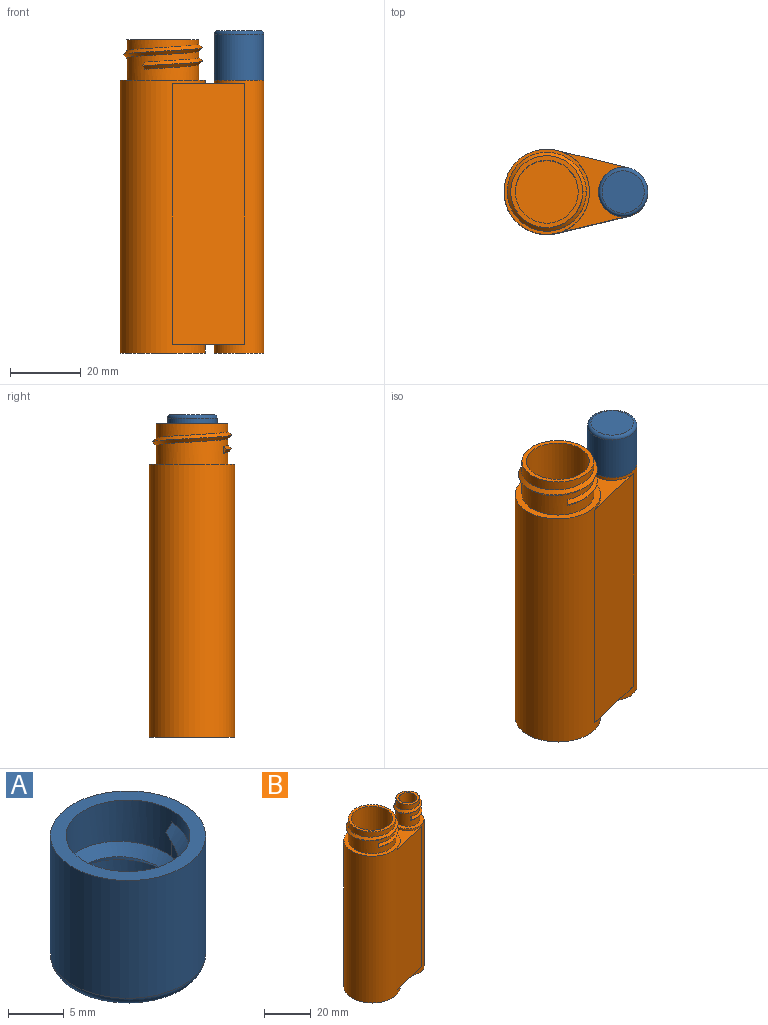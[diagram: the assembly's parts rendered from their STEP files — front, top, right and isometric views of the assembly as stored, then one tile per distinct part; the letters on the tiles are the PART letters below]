
ASSEMBLY  parts=2 mates=1
PART A: 12 faces, bbox 15.2x15.2x14 mm
  f0: cylinder r=6.99mm len=13.97mm, axis (0,0,-1), area 569.2mm2, adj f2,f3
  f1: plane 11.97x11.97mm, normal (0,0,-1), area 112.5mm2, adj f2
  f2: torus R=5.98mm, axis (0,0,1), area 65.4mm2, adj f0,f1
  f3: plane 13.97x13.97mm, normal (0,0,1), area 55.5mm2, adj f0,f11
  f4: plane 1.39x0.81mm, normal (0,1,0), area 0.5mm2, adj f5,f8,f11
  f5: bspline ~3.23x2.71mm, area 4.3mm2, adj f4,f6,f8,f10,f11
  f6: bspline ~12.89x11.16mm, area 55.6mm2, adj f5,f7,f8,f10
  f7: plane 2x0.87mm, normal (-0.87,0.5,0), area 1mm2, adj f6,f8,f10
  f8: bspline ~12.89x11.16mm, area 59.9mm2, adj f4,f5,f6,f7,f10,f11
  f9: plane 11.16x11.16mm, normal (0,0,1), area 97.8mm2, adj f10
  f10: cylinder r=5.58mm len=11.16mm, axis (0,0,-1), area 197mm2, adj f5,f6,f7,f8,f9,f11
  f11: cylinder r=5.58mm len=11.16mm, axis (0,0,-1), area 148.6mm2, adj f3,f4,f5,f8,f10
PART B: 28 faces, bbox 40.6x25.8x88.6 mm
  f0: cylinder r=6.99mm len=77.2mm, axis (0,0,-1), area 1527.3mm2, adj f2,f4,f5,f6,f7,f11
  f1: cylinder r=12.06mm len=77.2mm, axis (0,0,-1), area 3482.5mm2, adj f2,f3,f5,f6,f7,f8
  f2: plane 23.45x20.47mm, normal (0,0,1), area 117.4mm2, adj f0,f1,f6,f7
  f3: plane 24.13x24.13mm, normal (0,0,-1), area 457.3mm2, adj f1
  f4: plane 13.97x13.97mm, normal (0,0,-1), area 153.3mm2, adj f0
  f5: plane 23.45x20.47mm, normal (0,0,-1), area 117.4mm2, adj f0,f1,f6,f7
  f6: plane 73.66x20.37mm, normal (0.24,0.97,0), area 1545.7mm2, adj f0,f1,f2,f5
  f7: plane 73.66x20.42mm, normal (0.23,-0.97,0), area 1545.7mm2, adj f0,f1,f2,f5
  f8: plane 24.13x24.13mm, normal (0,0,1), area 133mm2, adj f1,f9
  f9: cylinder r=10.16mm len=20.32mm, axis (0,0,1), area 356.7mm2, adj f8,f10,f15,f16,f17
  f10: cylinder r=10.16mm len=20.32mm, axis (0,0,1), area 202.7mm2, adj f9,f14,f16,f22
  f11: plane 13.97x13.97mm, normal (0,0,1), area 72.2mm2, adj f0,f12
  f12: cylinder r=5.08mm len=10.16mm, axis (0,0,1), area 178.4mm2, adj f11,f13,f19,f20,f21
  f13: cylinder r=5.08mm len=10.16mm, axis (0,0,1), area 101.3mm2, adj f12,f18,f20,f25
  f14: plane 2x1mm, normal (0,1,0), area 1mm2, adj f10,f16,f17
  f15: plane 2x0.87mm, normal (-0.87,0.5,0), area 1mm2, adj f9,f16,f17
  f16: bspline ~25.77x22.32mm, area 126.4mm2, adj f9,f10,f14,f15,f17
  f17: bspline ~25.77x22.32mm, area 126.3mm2, adj f9,f14,f15,f16
  f18: plane 2x1mm, normal (0,1,0), area 1mm2, adj f13,f20,f21
  f19: plane 2x0.87mm, normal (-0.87,0.5,0), area 1mm2, adj f12,f20,f21
  f20: bspline ~14.04x12.16mm, area 66.3mm2, adj f12,f13,f18,f19,f21
  f21: bspline ~14.04x12.16mm, area 66.3mm2, adj f12,f18,f19,f20
  f22: plane 20.32x20.32mm, normal (0,0,1), area 76mm2, adj f10,f24
  f23: plane 17.78x17.78mm, normal (0,0,1), area 248.3mm2, adj f24
  f24: cylinder r=8.89mm len=86.09mm, axis (0,0,-1), area 4808.8mm2, adj f22,f23
  f25: plane 10.16x10.16mm, normal (0,0,1), area 35.5mm2, adj f13,f27
  f26: plane 7.62x7.62mm, normal (0,0,1), area 45.6mm2, adj f27
  f27: cylinder r=3.81mm len=86.09mm, axis (0,0,-1), area 2060.9mm2, adj f25,f26
PLACE A rot(axis=(1,0,0),180deg) t=(21.59,-0.09,120.63)mm
PLACE B t=(0,0,29.46)mm
MATE slider A.f10 <-> B.f0  axis (0,0,-1) through (21.59,-0.09,118.09)mm
